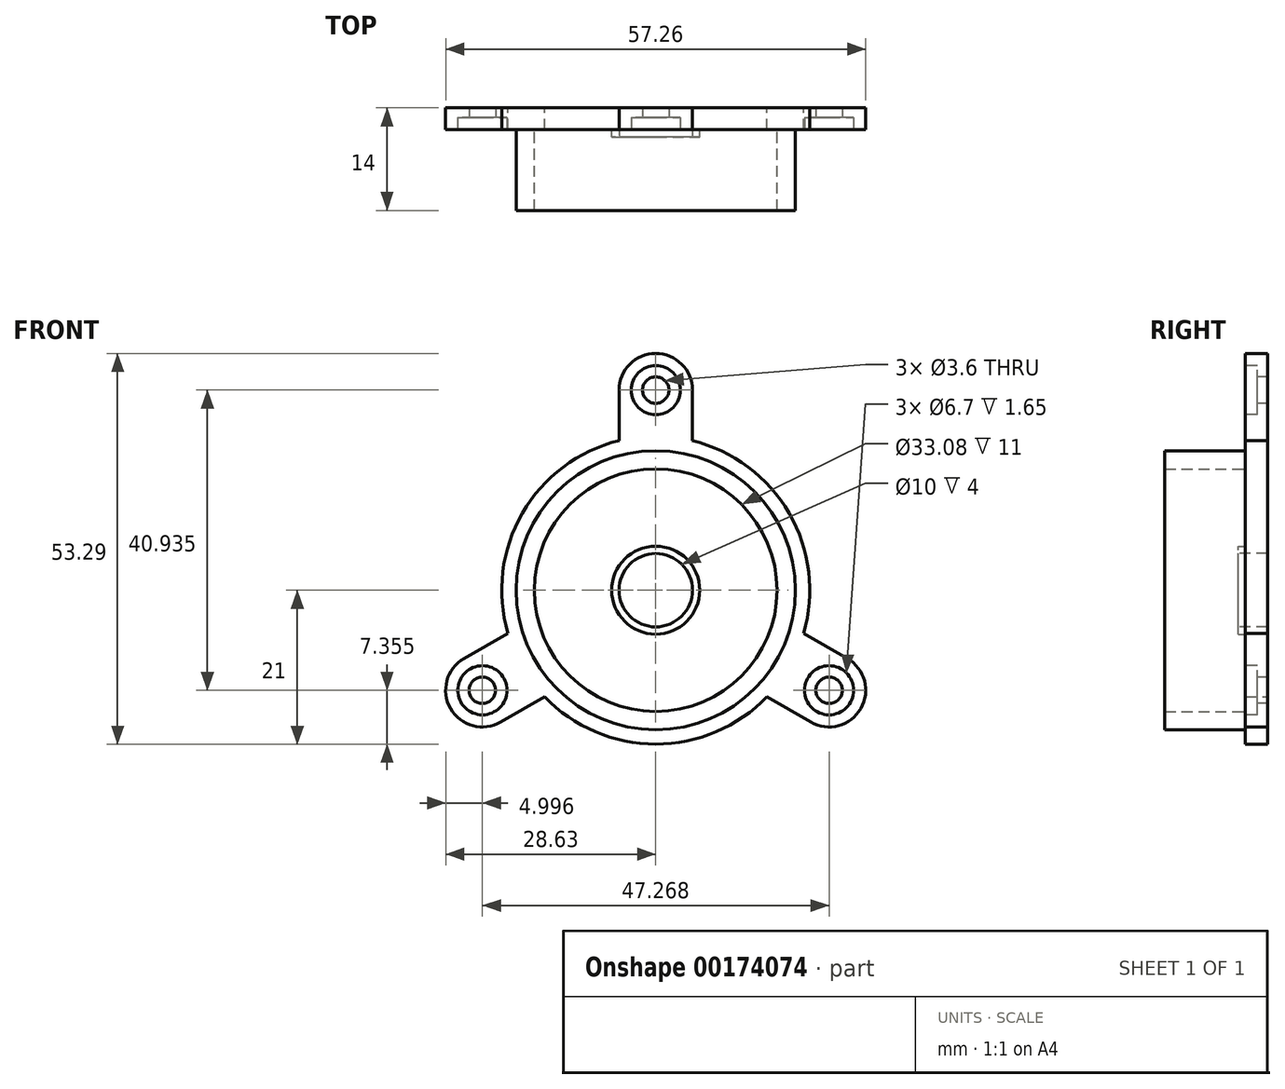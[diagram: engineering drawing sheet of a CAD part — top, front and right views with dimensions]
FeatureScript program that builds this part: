
annotation { "Feature Type Name" : "Feature", "Feature Type Description" : "" }
export const myFeature = defineFeature(function(context is Context, id is Id, definition is map)
    precondition{}
    {
        {
            var Q0;
            Q0=qCreatedBy(makeId("Front.planeOp"),FACE);
            var sketch = newSketch(context, id + "F0", { "sketchPlane" : qUnion([Q0])});
            skArc(sketch, "E0", {"start": v(-5, 20.4) * mm, "mid": v(-18.19, 10.5) * mm, "end": v(-20.16, -5.87) * mm});
            skLineSegment(sketch, "E1", {"start": v(-5, 20.4) * mm, "end": v(-5, 27.29) * mm});
            skLineSegment(sketch, "E2", {"start": v(5, 27.29) * mm, "end": v(5, 20.4) * mm});
            skArc(sketch, "E3", {"start": v(5, 27.29) * mm, "mid": v(0, 32.29) * mm, "end": v(-5, 27.29) * mm});
            skArc(sketch, "E4.1.0", {"start": v(-26.13, -9.31) * mm, "mid": v(-27.96, -16.14) * mm, "end": v(-21.13, -17.98) * mm});
            skLineSegment(sketch, "E4.1.1", {"start": v(-26.13, -9.31) * mm, "end": v(-20.16, -5.87) * mm});
            skLineSegment(sketch, "E4.1.2", {"start": v(-15.16, -14.53) * mm, "end": v(-21.13, -17.98) * mm});
            skArc(sketch, "E4.2.0", {"start": v(21.13, -17.98) * mm, "mid": v(27.96, -16.14) * mm, "end": v(26.13, -9.31) * mm});
            skLineSegment(sketch, "E4.2.1", {"start": v(21.13, -17.98) * mm, "end": v(15.16, -14.53) * mm});
            skLineSegment(sketch, "E4.2.2", {"start": v(20.16, -5.87) * mm, "end": v(26.13, -9.31) * mm});
            skArc(sketch, "E5.trimOffspring", {"start": v(-15.16, -14.53) * mm, "mid": v(0, -21) * mm, "end": v(15.16, -14.53) * mm});
            skArc(sketch, "E6.trimOffspring", {"start": v(20.16, -5.87) * mm, "mid": v(18.19, 10.5) * mm, "end": v(5, 20.4) * mm});
            skSolve(sketch);
        }
        {
            var Q0;
            Q0=makeQuery(id+"F0.imprint","IMPRINT",FACE,{"disambiguationData":[TD([[makeQuery(id+"F0.imprint","IMPRINT",EDGE,{"derivedFrom":sQuery(id+"F0.wireOp",EDGE,"E0")}),1.0]])]});
            extrude(context, id + "F1", {"entities" : qUnion([Q0]), "depth" : 3 * mm});
        }
        {
            var Q0;
            Q0=makeQuery(id+"F1.opExtrude","CAP_FACE",FACE,{"disambiguationData":[OSD([sQuery(id+"F0.wireOp",EDGE,"E0"),sQuery(id+"F0.wireOp",EDGE,"E1"),sQuery(id+"F0.wireOp",EDGE,"E2"),sQuery(id+"F0.wireOp",EDGE,"E3"),sQuery(id+"F0.wireOp",EDGE,"E4.1.0"),sQuery(id+"F0.wireOp",EDGE,"E4.1.1"),sQuery(id+"F0.wireOp",EDGE,"E4.1.2"),sQuery(id+"F0.wireOp",EDGE,"E4.2.0"),sQuery(id+"F0.wireOp",EDGE,"E4.2.1"),sQuery(id+"F0.wireOp",EDGE,"E4.2.2"),sQuery(id+"F0.wireOp",EDGE,"E5.trimOffspring"),sQuery(id+"F0.wireOp",EDGE,"E6.trimOffspring")])],"isStart":false});
            var sketch = newSketch(context, id + "F2", { "sketchPlane" : qUnion([Q0])});
            skCircle(sketch, "E7", {"center": v(0, 0) * mm, "radius": 19.03 * mm});
            skCircle(sketch, "E8", {"center": v(0, 0) * mm, "radius": 16.54 * mm});
            skSolve(sketch);
        }
        {
            var Q0;
            Q0=makeQuery(id+"F2.imprint","IMPRINT",FACE,{"disambiguationData":[TD([[makeQuery(id+"F2.imprint","IMPRINT",EDGE,{"derivedFrom":sQuery(id+"F2.wireOp",EDGE,"E7")}),1.0]])]});
            extrude(context, id + "F3", {"entities" : qUnion([Q0]), "operationType" : NewBodyOperationType.ADD, "depth" : 11 * mm});
        }
        {
            var Q0;
            Q0=makeQuery(id+"F3.boolean.opBoolean","SPLIT",FACE,{"disambiguationData":[TD([makeQuery(id+"F3.opExtrude","SWEPT_FACE",FACE,{"disambiguationData":[OSD([sQuery(id+"F2.wireOp",EDGE,"E8")])]})])],"derivedFrom":makeQuery(id+"F1.opExtrude","CAP_FACE",FACE,{"disambiguationData":[OSD([sQuery(id+"F0.wireOp",EDGE,"E0"),sQuery(id+"F0.wireOp",EDGE,"E1"),sQuery(id+"F0.wireOp",EDGE,"E2"),sQuery(id+"F0.wireOp",EDGE,"E3"),sQuery(id+"F0.wireOp",EDGE,"E4.1.0"),sQuery(id+"F0.wireOp",EDGE,"E4.1.1"),sQuery(id+"F0.wireOp",EDGE,"E4.1.2"),sQuery(id+"F0.wireOp",EDGE,"E4.2.0"),sQuery(id+"F0.wireOp",EDGE,"E4.2.1"),sQuery(id+"F0.wireOp",EDGE,"E4.2.2"),sQuery(id+"F0.wireOp",EDGE,"E5.trimOffspring"),sQuery(id+"F0.wireOp",EDGE,"E6.trimOffspring")])],"isStart":false})});
            var sketch = newSketch(context, id + "F4", { "sketchPlane" : qUnion([Q0])});
            skCircle(sketch, "E9", {"center": v(0, 0) * mm, "radius": 5 * mm});
            skSolve(sketch);
        }
        {
            var Q0;
            Q0=makeQuery(id+"F4.imprint","IMPRINT",FACE,{"disambiguationData":[TD([[makeQuery(id+"F4.imprint","IMPRINT",EDGE,{"derivedFrom":sQuery(id+"F4.wireOp",EDGE,"E9")}),1.0]])]});
            extrude(context, id + "F5", {"entities" : qUnion([Q0]), "operationType" : NewBodyOperationType.REMOVE, "endBound" : BoundingType.THROUGH_ALL, "oppositeDirection" : true, "depth" : 25 * mm});
        }
        {
            var Q0;
            Q0=makeQuery(id+"F3.boolean.opBoolean","SPLIT",FACE,{"disambiguationData":[TD([makeQuery(id+"F3.opExtrude","SWEPT_FACE",FACE,{"disambiguationData":[OSD([sQuery(id+"F2.wireOp",EDGE,"E8")])]})])],"derivedFrom":makeQuery(id+"F1.opExtrude","CAP_FACE",FACE,{"disambiguationData":[OSD([sQuery(id+"F0.wireOp",EDGE,"E0"),sQuery(id+"F0.wireOp",EDGE,"E1"),sQuery(id+"F0.wireOp",EDGE,"E2"),sQuery(id+"F0.wireOp",EDGE,"E3"),sQuery(id+"F0.wireOp",EDGE,"E4.1.0"),sQuery(id+"F0.wireOp",EDGE,"E4.1.1"),sQuery(id+"F0.wireOp",EDGE,"E4.1.2"),sQuery(id+"F0.wireOp",EDGE,"E4.2.0"),sQuery(id+"F0.wireOp",EDGE,"E4.2.1"),sQuery(id+"F0.wireOp",EDGE,"E4.2.2"),sQuery(id+"F0.wireOp",EDGE,"E5.trimOffspring"),sQuery(id+"F0.wireOp",EDGE,"E6.trimOffspring")])],"isStart":false})});
            var sketch = newSketch(context, id + "F6", { "sketchPlane" : qUnion([Q0])});
            skCircle(sketch, "E10", {"center": v(0, 0) * mm, "radius": 6 * mm});
            skSolve(sketch);
        }
        {
            var Q0;
            {var subQ0=sQuery(id+"F0.wireOp",EDGE,"E4.2.2");var subQ1=sQuery(id+"F0.wireOp",EDGE,"E4.2.0");var subQ2=sQuery(id+"F0.wireOp",EDGE,"E4.1.2");var subQ3=sQuery(id+"F0.wireOp",EDGE,"E4.1.1");var subQ4=sQuery(id+"F0.wireOp",EDGE,"E4.1.0");var subQ5=sQuery(id+"F0.wireOp",EDGE,"E0");var subQ6=sQuery(id+"F0.wireOp",EDGE,"E4.2.1");var subQ7=sQuery(id+"F0.wireOp",EDGE,"E1");var subQ8=sQuery(id+"F0.wireOp",EDGE,"E2");var subQ9=sQuery(id+"F0.wireOp",EDGE,"E3");var subQ10=sQuery(id+"F0.wireOp",EDGE,"E5.trimOffspring");var subQ11=sQuery(id+"F0.wireOp",EDGE,"E6.trimOffspring");Q0=makeQuery(id+"F3.boolean.opBoolean","SPLIT",FACE,{"disambiguationData":[TD([makeQuery(id+"F1.opExtrude","SWEPT_FACE",FACE,{"disambiguationData":[OSD([subQ5])]})])],"derivedFrom":makeQuery(id+"F1.opExtrude","CAP_FACE",FACE,{"disambiguationData":[OSD([subQ5,subQ7,subQ8,subQ9,subQ4,subQ3,subQ2,subQ1,subQ6,subQ0,subQ10,subQ11])],"isStart":false})});}
            var sketch = newSketch(context, id + "F7", { "sketchPlane" : qUnion([Q0])});
            skCircle(sketch, "E11", {"center": v(0, 27.29) * mm, "radius": 1.8 * mm});
            skCircle(sketch, "E12.1.0", {"center": v(-23.63, -13.64) * mm, "radius": 1.8 * mm});
            skCircle(sketch, "E12.2.0", {"center": v(23.63, -13.64) * mm, "radius": 1.8 * mm});
            skPoint(sketch, "E12.center", {"position": v(0, 0) * mm});
            skSolve(sketch);
        }
        {
            var Q0;
            Q0=makeQuery(id+"F7.imprint","IMPRINT",FACE,{"disambiguationData":[TD([[makeQuery(id+"F7.imprint","IMPRINT",EDGE,{"derivedFrom":sQuery(id+"F7.wireOp",EDGE,"E12.1.0")}),1.0]])]});
            var Q1;
            Q1=makeQuery(id+"F7.imprint","IMPRINT",FACE,{"disambiguationData":[TD([[makeQuery(id+"F7.imprint","IMPRINT",EDGE,{"derivedFrom":sQuery(id+"F7.wireOp",EDGE,"E12.2.0")}),1.0]])]});
            var Q2;
            Q2=makeQuery(id+"F7.imprint","IMPRINT",FACE,{"disambiguationData":[TD([[makeQuery(id+"F7.imprint","IMPRINT",EDGE,{"derivedFrom":sQuery(id+"F7.wireOp",EDGE,"E11")}),1.0]])]});
            extrude(context, id + "F8", {"entities" : qUnion([Q0, Q1, Q2]), "operationType" : NewBodyOperationType.REMOVE, "endBound" : BoundingType.THROUGH_ALL, "oppositeDirection" : true, "depth" : 25 * mm});
        }
        {
            var Q0;
            Q0=makeQuery(id+"F6.imprint","IMPRINT",FACE,{"disambiguationData":[TD([[makeQuery(id+"F6.imprint","IMPRINT",EDGE,{"derivedFrom":sQuery(id+"F6.wireOp",EDGE,"E10")}),1.0]])]});
            extrude(context, id + "F9", {"entities" : qUnion([Q0]), "operationType" : NewBodyOperationType.ADD, "depth" : 1 * mm});
        }
        {
            var Q0;
            {var subQ0=sQuery(id+"F0.wireOp",EDGE,"E4.2.2");var subQ1=sQuery(id+"F0.wireOp",EDGE,"E4.2.0");var subQ2=sQuery(id+"F0.wireOp",EDGE,"E4.1.2");var subQ3=sQuery(id+"F0.wireOp",EDGE,"E4.1.1");var subQ4=sQuery(id+"F0.wireOp",EDGE,"E4.1.0");var subQ5=sQuery(id+"F0.wireOp",EDGE,"E0");var subQ6=sQuery(id+"F0.wireOp",EDGE,"E4.2.1");var subQ7=sQuery(id+"F0.wireOp",EDGE,"E1");var subQ8=sQuery(id+"F0.wireOp",EDGE,"E2");var subQ9=sQuery(id+"F0.wireOp",EDGE,"E3");var subQ10=sQuery(id+"F0.wireOp",EDGE,"E5.trimOffspring");var subQ11=sQuery(id+"F0.wireOp",EDGE,"E6.trimOffspring");Q0=makeQuery(id+"F3.boolean.opBoolean","SPLIT",FACE,{"disambiguationData":[TD([makeQuery(id+"F1.opExtrude","SWEPT_FACE",FACE,{"disambiguationData":[OSD([subQ5])]})])],"derivedFrom":makeQuery(id+"F1.opExtrude","CAP_FACE",FACE,{"disambiguationData":[OSD([subQ5,subQ7,subQ8,subQ9,subQ4,subQ3,subQ2,subQ1,subQ6,subQ0,subQ10,subQ11])],"isStart":false})});}
            var sketch = newSketch(context, id + "F10", { "sketchPlane" : qUnion([Q0])});
            skCircle(sketch, "E13", {"center": v(0, 27.29) * mm, "radius": 3.35 * mm});
            skCircle(sketch, "E14.1.0", {"center": v(-23.63, -13.64) * mm, "radius": 3.35 * mm});
            skCircle(sketch, "E14.2.0", {"center": v(23.63, -13.64) * mm, "radius": 3.35 * mm});
            skPoint(sketch, "E14.center", {"position": v(0, 0) * mm});
            skSolve(sketch);
        }
        {
            var Q0;
            Q0=makeQuery(id+"F10.imprint","IMPRINT",FACE,{"disambiguationData":[TD([[makeQuery(id+"F10.imprint","IMPRINT",EDGE,{"derivedFrom":sQuery(id+"F10.wireOp",EDGE,"E13")}),1.0]])]});
            extrude(context, id + "F11", {"entities" : qUnion([Q0]), "operationType" : NewBodyOperationType.REMOVE, "oppositeDirection" : true, "depth" : 1.65 * mm});
        }
        {
            var Q0;
            {var subQ0=sQuery(id+"F0.wireOp",EDGE,"E4.2.2");var subQ1=sQuery(id+"F0.wireOp",EDGE,"E4.2.0");var subQ2=sQuery(id+"F0.wireOp",EDGE,"E4.1.2");var subQ3=sQuery(id+"F0.wireOp",EDGE,"E4.1.1");var subQ4=sQuery(id+"F0.wireOp",EDGE,"E4.1.0");var subQ5=sQuery(id+"F0.wireOp",EDGE,"E0");var subQ6=sQuery(id+"F0.wireOp",EDGE,"E4.2.1");var subQ7=sQuery(id+"F0.wireOp",EDGE,"E1");var subQ8=sQuery(id+"F0.wireOp",EDGE,"E2");var subQ9=sQuery(id+"F0.wireOp",EDGE,"E3");var subQ10=sQuery(id+"F0.wireOp",EDGE,"E5.trimOffspring");var subQ11=sQuery(id+"F0.wireOp",EDGE,"E6.trimOffspring");Q0=makeQuery(id+"F3.boolean.opBoolean","SPLIT",FACE,{"disambiguationData":[TD([makeQuery(id+"F1.opExtrude","SWEPT_FACE",FACE,{"disambiguationData":[OSD([subQ5])]})])],"derivedFrom":makeQuery(id+"F1.opExtrude","CAP_FACE",FACE,{"disambiguationData":[OSD([subQ5,subQ7,subQ8,subQ9,subQ4,subQ3,subQ2,subQ1,subQ6,subQ0,subQ10,subQ11])],"isStart":false})});}
            var sketch = newSketch(context, id + "F12", { "sketchPlane" : qUnion([Q0])});
            skCircle(sketch, "E15", {"center": v(-23.63, -13.64) * mm, "radius": 3.35 * mm});
            skCircle(sketch, "E16", {"center": v(23.63, -13.64) * mm, "radius": 3.35 * mm});
            skSolve(sketch);
        }
        {
            var Q0;
            Q0=makeQuery(id+"F12.imprint","IMPRINT",FACE,{"disambiguationData":[TD([[makeQuery(id+"F12.imprint","IMPRINT",EDGE,{"derivedFrom":sQuery(id+"F12.wireOp",EDGE,"E16")}),1.0]])]});
            var Q1;
            Q1=makeQuery(id+"F12.imprint","IMPRINT",FACE,{"disambiguationData":[TD([[makeQuery(id+"F12.imprint","IMPRINT",EDGE,{"derivedFrom":sQuery(id+"F12.wireOp",EDGE,"E15")}),1.0]])]});
            extrude(context, id + "F13", {"entities" : qUnion([Q0, Q1]), "operationType" : NewBodyOperationType.REMOVE, "oppositeDirection" : true, "depth" : 1.65 * mm});
        }
    });
